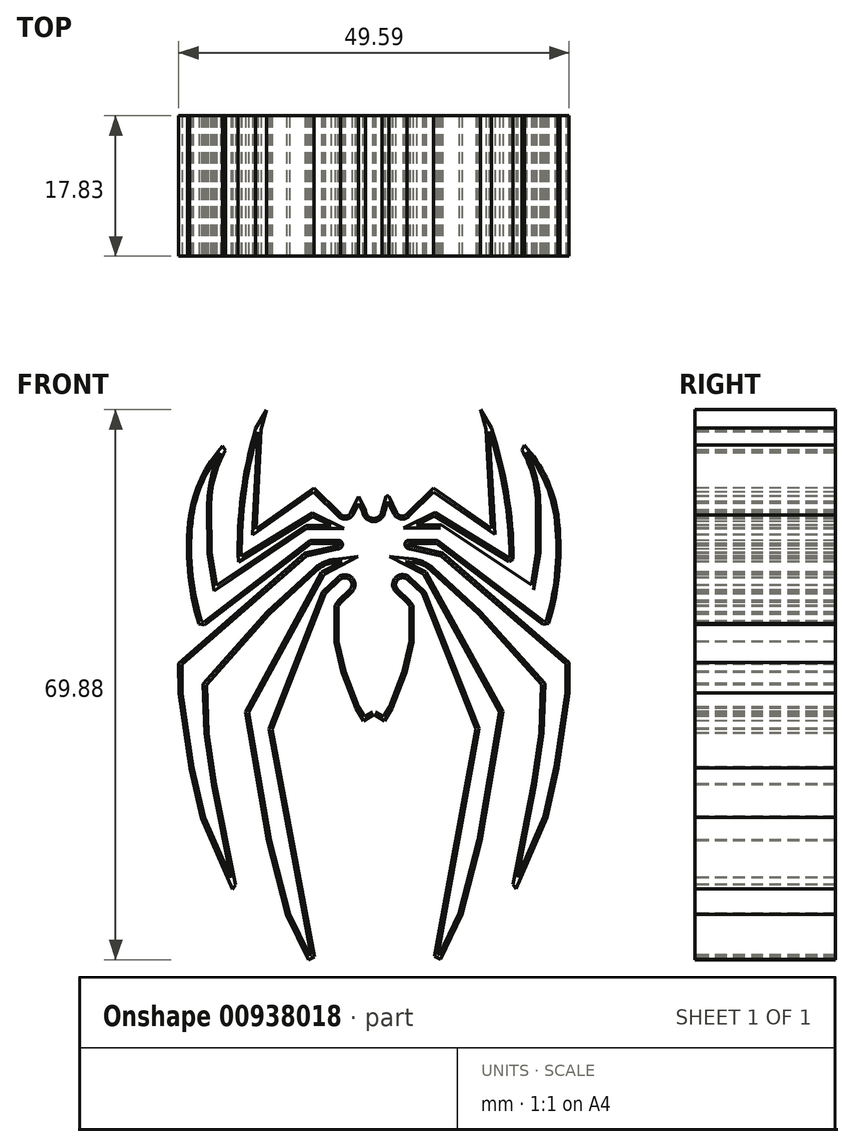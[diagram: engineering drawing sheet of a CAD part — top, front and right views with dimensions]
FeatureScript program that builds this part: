
annotation { "Feature Type Name" : "Feature", "Feature Type Description" : "" }
export const myFeature = defineFeature(function(context is Context, id is Id, definition is map)
    precondition{}
    {
        {
            var Q0;
            Q0=qCreatedBy(makeId("Front.planeOp"),FACE);
            var sketch = newSketch(context, id + "F0", { "sketchPlane" : qUnion([Q0])});
            skArc(sketch, "E0", {"start": v(10.3, 43.39) * mm, "mid": v(11.32, 42.32) * mm, "end": v(12.36, 43.36) * mm});
            skLineSegment(sketch, "E1", {"start": v(12.36, 43.36) * mm, "end": v(12.91, 45.08) * mm});
            skLineSegment(sketch, "E2", {"start": v(10.3, 43.39) * mm, "end": v(9.41, 45.08) * mm});
            skArc(sketch, "E3", {"start": v(13.25, 45.08) * mm, "mid": v(13.08, 45.2) * mm, "end": v(12.91, 45.08) * mm});
            skLineSegment(sketch, "E4", {"start": v(13.25, 45.08) * mm, "end": v(14.26, 43.06) * mm});
            skArc(sketch, "E5", {"start": v(14.26, 43.06) * mm, "mid": v(14.86, 42.62) * mm, "end": v(15.56, 42.87) * mm});
            skLineSegment(sketch, "E6", {"start": v(15.56, 42.87) * mm, "end": v(18.91, 46.2) * mm});
            skLineSegment(sketch, "E7", {"start": v(18.91, 46.2) * mm, "end": v(26.28, 41.06) * mm});
            skLineSegment(sketch, "E8", {"start": v(26.28, 41.06) * mm, "end": v(25.6, 53.69) * mm});
            skLineSegment(sketch, "E9", {"start": v(25.6, 53.69) * mm, "end": v(24.88, 56.14) * mm});
            skLineSegment(sketch, "E10", {"start": v(24.88, 56.14) * mm, "end": v(26.28, 53.79) * mm});
            skArc(sketch, "E11", {"start": v(29.06, 37.18) * mm, "mid": v(28.32, 45.6) * mm, "end": v(26.28, 53.79) * mm});
            skLineSegment(sketch, "E12", {"start": v(29.06, 37.18) * mm, "end": v(28.54, 36.84) * mm});
            skLineSegment(sketch, "E13", {"start": v(28.54, 36.84) * mm, "end": v(19.08, 42.61) * mm});
            skLineSegment(sketch, "E14", {"start": v(19.08, 42.61) * mm, "end": v(16.77, 41.46) * mm});
            skLineSegment(sketch, "E15", {"start": v(16.77, 41.46) * mm, "end": v(19.96, 41.46) * mm});
            skLineSegment(sketch, "E16", {"start": v(19.96, 41.46) * mm, "end": v(31.36, 33.86) * mm});
            skLineSegment(sketch, "E17", {"start": v(31.36, 33.86) * mm, "end": v(32.04, 38) * mm});
            skLineSegment(sketch, "E18", {"start": v(32.04, 38) * mm, "end": v(32.04, 43.9) * mm});
            skArc(sketch, "E19", {"start": v(32.04, 43.9) * mm, "mid": v(31.55, 47.6) * mm, "end": v(30.14, 51.03) * mm});
            skLineSegment(sketch, "E20", {"start": v(30.14, 51.03) * mm, "end": v(30.48, 51.61) * mm});
            skArc(sketch, "E21", {"start": v(34.72, 42.74) * mm, "mid": v(33.26, 47.5) * mm, "end": v(30.48, 51.61) * mm});
            skArc(sketch, "E22", {"start": v(33.56, 29) * mm, "mid": v(34.89, 35.8) * mm, "end": v(34.72, 42.74) * mm});
            skLineSegment(sketch, "E23", {"start": v(33.56, 29) * mm, "end": v(32.85, 28.84) * mm});
            skLineSegment(sketch, "E24", {"start": v(32.85, 28.84) * mm, "end": v(19.33, 39.16) * mm});
            skLineSegment(sketch, "E25", {"start": v(19.33, 39.16) * mm, "end": v(15.77, 39.16) * mm});
            skArc(sketch, "E26", {"start": v(15.77, 39.16) * mm, "mid": v(15.73, 38.94) * mm, "end": v(15.94, 38.86) * mm});
            skLineSegment(sketch, "E27", {"start": v(15.94, 38.86) * mm, "end": v(20.06, 37.93) * mm});
            skLineSegment(sketch, "E28", {"start": v(20.06, 37.93) * mm, "end": v(36.16, 24.01) * mm});
            skLineSegment(sketch, "E29", {"start": v(36.16, 24.01) * mm, "end": v(36.16, 20.15) * mm});
            skLineSegment(sketch, "E30", {"start": v(36.16, 20.15) * mm, "end": v(34.77, 10.65) * mm});
            skLineSegment(sketch, "E31", {"start": v(34.77, 10.65) * mm, "end": v(33.34, 4.32) * mm});
            skLineSegment(sketch, "E32", {"start": v(33.34, 4.32) * mm, "end": v(29.4, -4.75) * mm});
            skLineSegment(sketch, "E33", {"start": v(29.4, -4.75) * mm, "end": v(29.05, -4.2) * mm});
            skLineSegment(sketch, "E34", {"start": v(29.05, -4.2) * mm, "end": v(31.52, 8.6) * mm});
            skLineSegment(sketch, "E35", {"start": v(31.52, 8.6) * mm, "end": v(32.48, 15.1) * mm});
            skLineSegment(sketch, "E36", {"start": v(32.48, 15.1) * mm, "end": v(32.67, 21.21) * mm});
            skLineSegment(sketch, "E37", {"start": v(32.67, 21.21) * mm, "end": v(24.64, 30.19) * mm});
            skLineSegment(sketch, "E38", {"start": v(24.64, 30.19) * mm, "end": v(18.7, 35.66) * mm});
            skArc(sketch, "E39", {"start": v(18.7, 35.66) * mm, "mid": v(17.59, 36.4) * mm, "end": v(16.31, 36.75) * mm});
            skLineSegment(sketch, "E40", {"start": v(16.31, 36.75) * mm, "end": v(15.4, 36.86) * mm});
            skLineSegment(sketch, "E41", {"start": v(15.4, 36.86) * mm, "end": v(17.97, 35.54) * mm});
            skLineSegment(sketch, "E42", {"start": v(17.97, 35.54) * mm, "end": v(27.73, 17.79) * mm});
            skLineSegment(sketch, "E43", {"start": v(27.73, 17.79) * mm, "end": v(24.98, 1.38) * mm});
            skLineSegment(sketch, "E44", {"start": v(24.98, 1.38) * mm, "end": v(22.56, -7.98) * mm});
            skLineSegment(sketch, "E45", {"start": v(22.56, -7.98) * mm, "end": v(19.82, -13.7) * mm});
            skLineSegment(sketch, "E46", {"start": v(19.82, -13.7) * mm, "end": v(19.04, -13.34) * mm});
            skLineSegment(sketch, "E47", {"start": v(19.04, -13.34) * mm, "end": v(24.33, 15.59) * mm});
            skLineSegment(sketch, "E48", {"start": v(24.33, 15.59) * mm, "end": v(17.56, 32.78) * mm});
            skLineSegment(sketch, "E49", {"start": v(17.56, 32.78) * mm, "end": v(15.62, 34.56) * mm});
            skArc(sketch, "E50", {"start": v(15.62, 34.56) * mm, "mid": v(14.37, 34.51) * mm, "end": v(14.4, 33.26) * mm});
            skLineSegment(sketch, "E51", {"start": v(14.4, 33.26) * mm, "end": v(15.83, 31.92) * mm});
            skLineSegment(sketch, "E52", {"start": v(15.83, 31.92) * mm, "end": v(16.3, 31.27) * mm});
            skLineSegment(sketch, "E53", {"start": v(16.3, 31.27) * mm, "end": v(16.3, 26.63) * mm});
            skLineSegment(sketch, "E54", {"start": v(16.3, 26.63) * mm, "end": v(15.44, 22.78) * mm});
            skLineSegment(sketch, "E55", {"start": v(15.44, 22.78) * mm, "end": v(13.67, 18.2) * mm});
            skLineSegment(sketch, "E56", {"start": v(13.67, 18.2) * mm, "end": v(12.73, 16.61) * mm});
            skLineSegment(sketch, "E57", {"start": v(12.73, 16.61) * mm, "end": v(11.38, 17.4) * mm});
            skLineSegment(sketch, "E58.MirrorCS", {"start": v(9.41, 45.08) * mm, "end": v(8.4, 43.05) * mm});
            skArc(sketch, "E59.MirrorCS", {"start": v(8.4, 43.05) * mm, "mid": v(7.8, 42.61) * mm, "end": v(7.11, 42.86) * mm});
            skLineSegment(sketch, "E60.MirrorCS", {"start": v(7.11, 42.86) * mm, "end": v(3.74, 46.16) * mm});
            skLineSegment(sketch, "E61.MirrorCS", {"start": v(3.74, 46.16) * mm, "end": v(-3.6, 41) * mm});
            skLineSegment(sketch, "E62.MirrorCS", {"start": v(-3.6, 41) * mm, "end": v(-2.97, 53.64) * mm});
            skLineSegment(sketch, "E63.MirrorCS", {"start": v(-2.97, 53.64) * mm, "end": v(-2.26, 56.09) * mm});
            skLineSegment(sketch, "E64.MirrorCS", {"start": v(-2.26, 56.09) * mm, "end": v(-3.65, 53.73) * mm});
            skArc(sketch, "E65.MirrorCS", {"start": v(-5.85, 36.78) * mm, "mid": v(-5.43, 45.34) * mm, "end": v(-3.65, 53.73) * mm});
            skLineSegment(sketch, "E66.MirrorCS", {"start": v(-5.85, 36.78) * mm, "end": v(3.6, 42.59) * mm});
            skLineSegment(sketch, "E67.MirrorCS", {"start": v(3.6, 42.59) * mm, "end": v(5.9, 41.44) * mm});
            skLineSegment(sketch, "E68.MirrorCS", {"start": v(5.9, 41.44) * mm, "end": v(2.71, 41.43) * mm});
            skLineSegment(sketch, "E69.MirrorCS", {"start": v(2.71, 41.43) * mm, "end": v(-8.66, 33.79) * mm});
            skLineSegment(sketch, "E70.MirrorCS", {"start": v(-8.66, 33.79) * mm, "end": v(-9.35, 37.93) * mm});
            skLineSegment(sketch, "E71.MirrorCS", {"start": v(-9.35, 37.93) * mm, "end": v(-9.38, 43.83) * mm});
            skArc(sketch, "E72.MirrorCS", {"start": v(-9.38, 43.83) * mm, "mid": v(-8.9, 47.52) * mm, "end": v(-7.5, 50.96) * mm});
            skLineSegment(sketch, "E73.MirrorCS", {"start": v(-7.5, 50.96) * mm, "end": v(-7.85, 51.55) * mm});
            skArc(sketch, "E74.MirrorCS", {"start": v(-12.05, 42.65) * mm, "mid": v(-10.61, 47.41) * mm, "end": v(-7.85, 51.55) * mm});
            skArc(sketch, "E75.MirrorCS", {"start": v(-10.85, 28.92) * mm, "mid": v(-12.2, 35.72) * mm, "end": v(-12.05, 42.65) * mm});
            skLineSegment(sketch, "E76.MirrorCS", {"start": v(-10.85, 28.92) * mm, "end": v(-10.13, 28.77) * mm});
            skLineSegment(sketch, "E77.MirrorCS", {"start": v(-10.13, 28.77) * mm, "end": v(3.35, 39.13) * mm});
            skLineSegment(sketch, "E78.MirrorCS", {"start": v(3.35, 39.13) * mm, "end": v(6.91, 39.14) * mm});
            skArc(sketch, "E79.MirrorCS", {"start": v(6.91, 39.14) * mm, "mid": v(6.95, 38.92) * mm, "end": v(6.74, 38.85) * mm});
            skLineSegment(sketch, "E80.MirrorCS", {"start": v(6.74, 38.85) * mm, "end": v(2.62, 37.9) * mm});
            skLineSegment(sketch, "E81.MirrorCS", {"start": v(2.62, 37.9) * mm, "end": v(-13.43, 23.92) * mm});
            skLineSegment(sketch, "E82.MirrorCS", {"start": v(-13.43, 23.92) * mm, "end": v(-13.41, 20.06) * mm});
            skLineSegment(sketch, "E83.MirrorCS", {"start": v(-13.41, 20.06) * mm, "end": v(-11.99, 10.57) * mm});
            skLineSegment(sketch, "E84.MirrorCS", {"start": v(-11.99, 10.57) * mm, "end": v(-10.54, 4.24) * mm});
            skLineSegment(sketch, "E85.MirrorCS", {"start": v(-10.54, 4.24) * mm, "end": v(-6.57, -4.82) * mm});
            skLineSegment(sketch, "E86.MirrorCS", {"start": v(-6.57, -4.82) * mm, "end": v(-6.22, -4.26) * mm});
            skLineSegment(sketch, "E87.MirrorCS", {"start": v(-6.22, -4.26) * mm, "end": v(-8.73, 8.52) * mm});
            skLineSegment(sketch, "E88.MirrorCS", {"start": v(-8.73, 8.52) * mm, "end": v(-9.72, 15.02) * mm});
            skLineSegment(sketch, "E89.MirrorCS", {"start": v(-9.72, 15.02) * mm, "end": v(-9.93, 21.14) * mm});
            skLineSegment(sketch, "E90.MirrorCS", {"start": v(-9.93, 21.14) * mm, "end": v(-1.93, 30.14) * mm});
            skLineSegment(sketch, "E91.MirrorCS", {"start": v(-1.93, 30.14) * mm, "end": v(4, 35.64) * mm});
            skArc(sketch, "E92.MirrorCS", {"start": v(4, 35.64) * mm, "mid": v(5.1, 36.38) * mm, "end": v(6.37, 36.74) * mm});
            skLineSegment(sketch, "E93.MirrorCS", {"start": v(6.37, 36.74) * mm, "end": v(7.3, 36.84) * mm});
            skLineSegment(sketch, "E94.MirrorCS", {"start": v(7.3, 36.84) * mm, "end": v(4.72, 35.52) * mm});
            skLineSegment(sketch, "E95.MirrorCS", {"start": v(4.72, 35.52) * mm, "end": v(-4.98, 17.73) * mm});
            skLineSegment(sketch, "E96.MirrorCS", {"start": v(-4.98, 17.73) * mm, "end": v(-2.17, 1.33) * mm});
            skLineSegment(sketch, "E97.MirrorCS", {"start": v(-2.17, 1.33) * mm, "end": v(0.29, -8.02) * mm});
            skLineSegment(sketch, "E98.MirrorCS", {"start": v(0.29, -8.02) * mm, "end": v(3.05, -13.74) * mm});
            skLineSegment(sketch, "E99.MirrorCS", {"start": v(3.05, -13.74) * mm, "end": v(3.83, -13.37) * mm});
            skLineSegment(sketch, "E100.MirrorCS", {"start": v(3.83, -13.37) * mm, "end": v(-1.57, 15.54) * mm});
            skLineSegment(sketch, "E101.MirrorCS", {"start": v(-1.57, 15.54) * mm, "end": v(5.15, 32.75) * mm});
            skLineSegment(sketch, "E102.MirrorCS", {"start": v(5.15, 32.75) * mm, "end": v(7.08, 34.54) * mm});
            skArc(sketch, "E103.MirrorCS", {"start": v(7.08, 34.54) * mm, "mid": v(8.33, 34.5) * mm, "end": v(8.3, 33.25) * mm});
            skLineSegment(sketch, "E104.MirrorCS", {"start": v(8.3, 33.25) * mm, "end": v(6.87, 31.9) * mm});
            skLineSegment(sketch, "E105.MirrorCS", {"start": v(6.87, 31.9) * mm, "end": v(6.4, 31.25) * mm});
            skLineSegment(sketch, "E106.MirrorCS", {"start": v(6.4, 31.25) * mm, "end": v(6.42, 26.6) * mm});
            skLineSegment(sketch, "E107.MirrorCS", {"start": v(6.42, 26.6) * mm, "end": v(7.3, 22.76) * mm});
            skLineSegment(sketch, "E108.MirrorCS", {"start": v(7.3, 22.76) * mm, "end": v(9.08, 18.2) * mm});
            skLineSegment(sketch, "E109.MirrorCS", {"start": v(9.08, 18.2) * mm, "end": v(10.03, 16.6) * mm});
            skLineSegment(sketch, "E110.MirrorCS", {"start": v(10.03, 16.6) * mm, "end": v(11.37, 17.4) * mm});
            skLineSegment(sketch, "E111.0", {"start": v(12.6, 17.14) * mm, "end": v(11.58, 17.74) * mm});
            skLineSegment(sketch, "E111.1", {"start": v(13.32, 18.38) * mm, "end": v(12.6, 17.14) * mm});
            skLineSegment(sketch, "E111.2", {"start": v(15.07, 22.89) * mm, "end": v(13.32, 18.38) * mm});
            skLineSegment(sketch, "E111.3", {"start": v(15.92, 26.67) * mm, "end": v(15.07, 22.89) * mm});
            skLineSegment(sketch, "E111.4", {"start": v(15.92, 31.14) * mm, "end": v(15.92, 26.67) * mm});
            skLineSegment(sketch, "E111.5", {"start": v(15.54, 31.66) * mm, "end": v(15.92, 31.14) * mm});
            skLineSegment(sketch, "E111.6", {"start": v(3.7, 45.66) * mm, "end": v(-4.03, 40.23) * mm});
            skLineSegment(sketch, "E111.7", {"start": v(-4.03, 40.23) * mm, "end": v(-3.38, 53.3) * mm});
            skArc(sketch, "E111.8", {"start": v(-5.48, 37.46) * mm, "mid": v(-5.02, 45.46) * mm, "end": v(-3.38, 53.3) * mm});
            skLineSegment(sketch, "E111.9", {"start": v(-5.48, 37.46) * mm, "end": v(3.57, 43.03) * mm});
            skLineSegment(sketch, "E111.10", {"start": v(3.57, 43.03) * mm, "end": v(7.54, 41.06) * mm});
            skLineSegment(sketch, "E111.11", {"start": v(7.54, 41.06) * mm, "end": v(2.83, 41.04) * mm});
            skLineSegment(sketch, "E111.12", {"start": v(2.83, 41.04) * mm, "end": v(-8.94, 33.13) * mm});
            skLineSegment(sketch, "E111.13", {"start": v(-8.94, 33.13) * mm, "end": v(-9.74, 37.9) * mm});
            skLineSegment(sketch, "E111.14", {"start": v(-9.74, 37.9) * mm, "end": v(-9.76, 43.83) * mm});
            skArc(sketch, "E111.15", {"start": v(-9.76, 43.83) * mm, "mid": v(-9.35, 47.34) * mm, "end": v(-8.1, 50.66) * mm});
            skArc(sketch, "E111.16", {"start": v(-11.67, 42.6) * mm, "mid": v(-10.43, 46.87) * mm, "end": v(-8.1, 50.66) * mm});
            skArc(sketch, "E111.17", {"start": v(-10.55, 29.25) * mm, "mid": v(-11.82, 35.86) * mm, "end": v(-11.67, 42.6) * mm});
            skLineSegment(sketch, "E111.18", {"start": v(-10.55, 29.25) * mm, "end": v(-10.23, 29.18) * mm});
            skLineSegment(sketch, "E111.19", {"start": v(-10.23, 29.18) * mm, "end": v(3.22, 39.52) * mm});
            skLineSegment(sketch, "E111.20", {"start": v(3.22, 39.52) * mm, "end": v(7, 39.53) * mm});
            skArc(sketch, "E111.21", {"start": v(7, 39.53) * mm, "mid": v(7.35, 38.88) * mm, "end": v(6.75, 38.45) * mm});
            skLineSegment(sketch, "E111.22", {"start": v(6.75, 38.45) * mm, "end": v(2.8, 37.55) * mm});
            skLineSegment(sketch, "E111.23", {"start": v(2.8, 37.55) * mm, "end": v(-13.04, 23.75) * mm});
            skLineSegment(sketch, "E111.24", {"start": v(-13.04, 23.75) * mm, "end": v(-13.03, 20.1) * mm});
            skLineSegment(sketch, "E111.25", {"start": v(-13.03, 20.1) * mm, "end": v(-11.6, 10.64) * mm});
            skLineSegment(sketch, "E111.26", {"start": v(-11.6, 10.64) * mm, "end": v(-10.17, 4.36) * mm});
            skLineSegment(sketch, "E111.27", {"start": v(-10.17, 4.36) * mm, "end": v(-6.79, -3.36) * mm});
            skLineSegment(sketch, "E111.28", {"start": v(-6.79, -3.36) * mm, "end": v(-9.11, 8.45) * mm});
            skLineSegment(sketch, "E111.29", {"start": v(-9.11, 8.45) * mm, "end": v(-10.1, 14.98) * mm});
            skLineSegment(sketch, "E111.30", {"start": v(-1.97, 15.58) * mm, "end": v(4.82, 32.98) * mm});
            skLineSegment(sketch, "E111.31", {"start": v(4.82, 32.98) * mm, "end": v(6.81, 34.83) * mm});
            skArc(sketch, "E111.32", {"start": v(6.81, 34.83) * mm, "mid": v(8.6, 34.76) * mm, "end": v(8.56, 32.97) * mm});
            skLineSegment(sketch, "E111.33", {"start": v(8.56, 32.97) * mm, "end": v(7.17, 31.64) * mm});
            skLineSegment(sketch, "E111.34", {"start": v(7.17, 31.64) * mm, "end": v(6.8, 31.13) * mm});
            skLineSegment(sketch, "E111.35", {"start": v(6.8, 31.13) * mm, "end": v(6.8, 26.65) * mm});
            skLineSegment(sketch, "E111.36", {"start": v(10.16, 17.14) * mm, "end": v(11.17, 17.74) * mm});
            skLineSegment(sketch, "E111.37", {"start": v(9.43, 18.37) * mm, "end": v(10.16, 17.14) * mm});
            skLineSegment(sketch, "E111.38", {"start": v(7.67, 22.87) * mm, "end": v(9.43, 18.37) * mm});
            skLineSegment(sketch, "E111.39", {"start": v(6.8, 26.65) * mm, "end": v(7.67, 22.87) * mm});
            skLineSegment(sketch, "E111.40", {"start": v(3.4, -13.15) * mm, "end": v(-1.97, 15.58) * mm});
            skLineSegment(sketch, "E111.41", {"start": v(3.23, -13.22) * mm, "end": v(3.4, -13.15) * mm});
            skLineSegment(sketch, "E111.42", {"start": v(0.65, -7.88) * mm, "end": v(3.23, -13.22) * mm});
            skLineSegment(sketch, "E111.43", {"start": v(-1.79, 1.42) * mm, "end": v(0.65, -7.88) * mm});
            skLineSegment(sketch, "E111.44", {"start": v(-4.57, 17.66) * mm, "end": v(-1.79, 1.42) * mm});
            skLineSegment(sketch, "E111.45", {"start": v(5, 35.23) * mm, "end": v(-4.57, 17.66) * mm});
            skLineSegment(sketch, "E111.46", {"start": v(9.36, 37.48) * mm, "end": v(5, 35.23) * mm});
            skLineSegment(sketch, "E111.47", {"start": v(6.33, 37.12) * mm, "end": v(9.36, 37.48) * mm});
            skArc(sketch, "E111.48", {"start": v(3.74, 35.92) * mm, "mid": v(4.94, 36.73) * mm, "end": v(6.33, 37.12) * mm});
            skLineSegment(sketch, "E111.49", {"start": v(-2.2, 30.41) * mm, "end": v(3.74, 35.92) * mm});
            skLineSegment(sketch, "E111.50", {"start": v(-10.32, 21.28) * mm, "end": v(-2.2, 30.41) * mm});
            skLineSegment(sketch, "E111.51", {"start": v(-10.1, 14.98) * mm, "end": v(-10.32, 21.28) * mm});
            skLineSegment(sketch, "E111.52", {"start": v(6.83, 42.59) * mm, "end": v(3.7, 45.66) * mm});
            skArc(sketch, "E111.53", {"start": v(8.75, 42.88) * mm, "mid": v(7.87, 42.23) * mm, "end": v(6.83, 42.59) * mm});
            skLineSegment(sketch, "E111.54", {"start": v(9.42, 44.23) * mm, "end": v(8.75, 42.88) * mm});
            skLineSegment(sketch, "E111.55", {"start": v(9.92, 43.29) * mm, "end": v(9.42, 44.23) * mm});
            skArc(sketch, "E111.56", {"start": v(9.92, 43.29) * mm, "mid": v(11.33, 41.93) * mm, "end": v(12.75, 43.3) * mm});
            skLineSegment(sketch, "E111.57", {"start": v(12.75, 43.3) * mm, "end": v(13.12, 44.46) * mm});
            skLineSegment(sketch, "E111.58", {"start": v(13.12, 44.46) * mm, "end": v(13.91, 42.88) * mm});
            skArc(sketch, "E111.59", {"start": v(13.91, 42.88) * mm, "mid": v(14.8, 42.24) * mm, "end": v(15.83, 42.6) * mm});
            skLineSegment(sketch, "E111.60", {"start": v(15.83, 42.6) * mm, "end": v(18.96, 45.69) * mm});
            skLineSegment(sketch, "E111.61", {"start": v(18.96, 45.69) * mm, "end": v(26.7, 40.29) * mm});
            skLineSegment(sketch, "E111.62", {"start": v(26.7, 40.29) * mm, "end": v(26, 53.39) * mm});
            skArc(sketch, "E111.63", {"start": v(28.67, 37.39) * mm, "mid": v(27.94, 45.49) * mm, "end": v(26, 53.39) * mm});
            skLineSegment(sketch, "E111.64", {"start": v(28.67, 37.39) * mm, "end": v(28.53, 37.3) * mm});
            skLineSegment(sketch, "E111.65", {"start": v(28.53, 37.3) * mm, "end": v(19.1, 43.06) * mm});
            skLineSegment(sketch, "E111.66", {"start": v(19.1, 43.06) * mm, "end": v(15.13, 41.07) * mm});
            skLineSegment(sketch, "E111.67", {"start": v(15.13, 41.07) * mm, "end": v(19.84, 41.07) * mm});
            skLineSegment(sketch, "E111.68", {"start": v(19.84, 41.07) * mm, "end": v(31.64, 33.2) * mm});
            skLineSegment(sketch, "E111.69", {"start": v(31.64, 33.2) * mm, "end": v(32.42, 37.97) * mm});
            skLineSegment(sketch, "E111.70", {"start": v(32.42, 37.97) * mm, "end": v(32.42, 43.9) * mm});
            skArc(sketch, "E111.71", {"start": v(32.42, 43.9) * mm, "mid": v(32, 47.42) * mm, "end": v(30.74, 50.73) * mm});
            skArc(sketch, "E111.72", {"start": v(34.34, 42.68) * mm, "mid": v(33.09, 46.95) * mm, "end": v(30.74, 50.73) * mm});
            skArc(sketch, "E111.73", {"start": v(33.26, 29.33) * mm, "mid": v(34.51, 35.95) * mm, "end": v(34.34, 42.68) * mm});
            skLineSegment(sketch, "E111.74", {"start": v(33.26, 29.33) * mm, "end": v(32.94, 29.26) * mm});
            skLineSegment(sketch, "E111.75", {"start": v(32.94, 29.26) * mm, "end": v(19.46, 39.54) * mm});
            skLineSegment(sketch, "E111.76", {"start": v(19.46, 39.54) * mm, "end": v(15.67, 39.54) * mm});
            skArc(sketch, "E111.77", {"start": v(15.67, 39.54) * mm, "mid": v(15.33, 38.89) * mm, "end": v(15.94, 38.47) * mm});
            skLineSegment(sketch, "E111.78", {"start": v(15.94, 38.47) * mm, "end": v(19.88, 37.58) * mm});
            skLineSegment(sketch, "E111.79", {"start": v(19.88, 37.58) * mm, "end": v(35.77, 23.83) * mm});
            skLineSegment(sketch, "E111.80", {"start": v(35.77, 23.83) * mm, "end": v(35.77, 20.18) * mm});
            skLineSegment(sketch, "E111.81", {"start": v(35.77, 20.18) * mm, "end": v(34.39, 10.72) * mm});
            skLineSegment(sketch, "E111.82", {"start": v(34.39, 10.72) * mm, "end": v(32.97, 4.44) * mm});
            skLineSegment(sketch, "E111.83", {"start": v(32.97, 4.44) * mm, "end": v(29.62, -3.3) * mm});
            skLineSegment(sketch, "E111.84", {"start": v(29.62, -3.3) * mm, "end": v(31.9, 8.53) * mm});
            skLineSegment(sketch, "E111.85", {"start": v(31.9, 8.53) * mm, "end": v(32.87, 15.06) * mm});
            skLineSegment(sketch, "E111.86", {"start": v(32.87, 15.06) * mm, "end": v(33.07, 21.36) * mm});
            skLineSegment(sketch, "E111.87", {"start": v(33.07, 21.36) * mm, "end": v(24.92, 30.46) * mm});
            skLineSegment(sketch, "E111.88", {"start": v(24.92, 30.46) * mm, "end": v(18.96, 35.95) * mm});
            skArc(sketch, "E111.89", {"start": v(18.96, 35.95) * mm, "mid": v(17.75, 36.75) * mm, "end": v(16.36, 37.14) * mm});
            skLineSegment(sketch, "E111.90", {"start": v(16.36, 37.14) * mm, "end": v(13.32, 37.49) * mm});
            skLineSegment(sketch, "E111.91", {"start": v(13.32, 37.49) * mm, "end": v(17.69, 35.25) * mm});
            skLineSegment(sketch, "E111.92", {"start": v(17.69, 35.25) * mm, "end": v(27.33, 17.72) * mm});
            skLineSegment(sketch, "E111.93", {"start": v(27.33, 17.72) * mm, "end": v(24.6, 1.46) * mm});
            skLineSegment(sketch, "E111.94", {"start": v(24.6, 1.46) * mm, "end": v(22.2, -7.85) * mm});
            skLineSegment(sketch, "E111.95", {"start": v(22.2, -7.85) * mm, "end": v(19.63, -13.2) * mm});
            skLineSegment(sketch, "E111.96", {"start": v(19.63, -13.2) * mm, "end": v(19.47, -13.12) * mm});
            skLineSegment(sketch, "E111.97", {"start": v(19.47, -13.12) * mm, "end": v(24.73, 15.62) * mm});
            skLineSegment(sketch, "E111.98", {"start": v(24.73, 15.62) * mm, "end": v(17.88, 33) * mm});
            skLineSegment(sketch, "E111.99", {"start": v(17.88, 33) * mm, "end": v(15.88, 34.84) * mm});
            skArc(sketch, "E111.100", {"start": v(15.88, 34.84) * mm, "mid": v(14.09, 34.77) * mm, "end": v(14.14, 32.98) * mm});
            skLineSegment(sketch, "E111.101", {"start": v(14.14, 32.98) * mm, "end": v(15.54, 31.66) * mm});
            skSolve(sketch);
        }
        {
            var Q0;
            Q0 = qSketchRegion(id + "F0", true);
            var Q1;
            Q1=sQuery(id+"F0.wireOp",EDGE,"E111.72");
            var Q2;
            Q2=sQuery(id+"F0.wireOp",EDGE,"E21");
            var Q3;
            Q3=sQuery(id+"F0.wireOp",EDGE,"E111.73");
            var Q4;
            Q4=sQuery(id+"F0.wireOp",EDGE,"E22");
            var Q5;
            Q5=sQuery(id+"F0.wireOp",EDGE,"E111.71");
            var Q6;
            Q6=sQuery(id+"F0.wireOp",EDGE,"E20");
            var Q7;
            Q7=sQuery(id+"F0.wireOp",EDGE,"E111.45");
            var Q8;
            Q8=sQuery(id+"F0.wireOp",EDGE,"E111.93");
            var Q9;
            Q9=sQuery(id+"F0.wireOp",EDGE,"E53");
            var Q10;
            Q10=sQuery(id+"F0.wireOp",EDGE,"E111.6");
            var Q11;
            Q11=sQuery(id+"F0.wireOp",EDGE,"E81.MirrorCS");
            var Q12;
            Q12=sQuery(id+"F0.wireOp",EDGE,"E111.2");
            var Q13;
            Q13=sQuery(id+"F0.wireOp",EDGE,"E17");
            var Q14;
            Q14=sQuery(id+"F0.wireOp",EDGE,"E111.30");
            var Q15;
            Q15=sQuery(id+"F0.wireOp",EDGE,"E111.69");
            var Q16;
            Q16=sQuery(id+"F0.wireOp",EDGE,"E29");
            var Q17;
            Q17=sQuery(id+"F0.wireOp",EDGE,"E111.13");
            var Q18;
            Q18=sQuery(id+"F0.wireOp",EDGE,"E111.98");
            var Q19;
            Q19=sQuery(id+"F0.wireOp",EDGE,"E111.94");
            var Q20;
            Q20=sQuery(id+"F0.wireOp",EDGE,"E37");
            var Q21;
            Q21=sQuery(id+"F0.wireOp",EDGE,"E111.25");
            var Q22;
            Q22=sQuery(id+"F0.wireOp",EDGE,"E24");
            var Q23;
            Q23=sQuery(id+"F0.wireOp",EDGE,"E111.50");
            var Q24;
            Q24=sQuery(id+"F0.wireOp",EDGE,"E111.38");
            var Q25;
            Q25=sQuery(id+"F0.wireOp",EDGE,"E97.MirrorCS");
            var Q26;
            Q26=sQuery(id+"F0.wireOp",EDGE,"E16");
            var Q27;
            Q27=sQuery(id+"F0.wireOp",EDGE,"E48");
            var Q28;
            Q28=sQuery(id+"F0.wireOp",EDGE,"E85.MirrorCS");
            var Q29;
            Q29=sQuery(id+"F0.wireOp",EDGE,"E32");
            var Q30;
            Q30=sQuery(id+"F0.wireOp",EDGE,"E108.MirrorCS");
            var Q31;
            Q31=sQuery(id+"F0.wireOp",EDGE,"E111.14");
            var Q32;
            Q32=sQuery(id+"F0.wireOp",EDGE,"E111.29");
            var Q33;
            Q33=sQuery(id+"F0.wireOp",EDGE,"E111.62");
            var Q34;
            Q34=sQuery(id+"F0.wireOp",EDGE,"E65.MirrorCS");
            var Q35;
            Q35=sQuery(id+"F0.wireOp",EDGE,"E44");
            var Q36;
            Q36=sQuery(id+"F0.wireOp",EDGE,"E96.MirrorCS");
            var Q37;
            Q37=sQuery(id+"F0.wireOp",EDGE,"E111.15");
            var Q38;
            Q38=sQuery(id+"F0.wireOp",EDGE,"E55");
            var Q39;
            Q39=sQuery(id+"F0.wireOp",EDGE,"E88.MirrorCS");
            var Q40;
            Q40=sQuery(id+"F0.wireOp",EDGE,"E72.MirrorCS");
            var Q41;
            Q41=sQuery(id+"F0.wireOp",EDGE,"E111.85");
            var Q42;
            Q42=sQuery(id+"F0.wireOp",EDGE,"E61.MirrorCS");
            var Q43;
            Q43=sQuery(id+"F0.wireOp",EDGE,"E77.MirrorCS");
            var Q44;
            Q44=sQuery(id+"F0.wireOp",EDGE,"E111.8");
            var Q45;
            Q45=sQuery(id+"F0.wireOp",EDGE,"E101.MirrorCS");
            var Q46;
            Q46=sQuery(id+"F0.wireOp",EDGE,"E111.24");
            var Q47;
            Q47=sQuery(id+"F0.wireOp",EDGE,"E111.95");
            var Q48;
            Q48=sQuery(id+"F0.wireOp",EDGE,"E111.82");
            var Q49;
            Q49=sQuery(id+"F0.wireOp",EDGE,"E62.MirrorCS");
            var Q50;
            Q50=sQuery(id+"F0.wireOp",EDGE,"E69.MirrorCS");
            var Q51;
            Q51=sQuery(id+"F0.wireOp",EDGE,"E84.MirrorCS");
            var Q52;
            Q52=sQuery(id+"F0.wireOp",EDGE,"E45");
            var Q53;
            Q53=sQuery(id+"F0.wireOp",EDGE,"E111.88");
            var Q54;
            Q54=sQuery(id+"F0.wireOp",EDGE,"E36");
            var Q55;
            Q55=sQuery(id+"F0.wireOp",EDGE,"E100.MirrorCS");
            var Q56;
            Q56=sQuery(id+"F0.wireOp",EDGE,"E111.79");
            var Q57;
            Q57=sQuery(id+"F0.wireOp",EDGE,"E111.86");
            var Q58;
            Q58=sQuery(id+"F0.wireOp",EDGE,"E30");
            var Q59;
            Q59=sQuery(id+"F0.wireOp",EDGE,"E111.9");
            var Q60;
            Q60=sQuery(id+"F0.wireOp",EDGE,"E111.40");
            var Q61;
            Q61=sQuery(id+"F0.wireOp",EDGE,"E111.61");
            var Q62;
            Q62=sQuery(id+"F0.wireOp",EDGE,"E111.70");
            var Q63;
            Q63=sQuery(id+"F0.wireOp",EDGE,"E11");
            var Q64;
            Q64=sQuery(id+"F0.wireOp",EDGE,"E111.23");
            var Q65;
            Q65=sQuery(id+"F0.wireOp",EDGE,"E31");
            var Q66;
            Q66=sQuery(id+"F0.wireOp",EDGE,"E35");
            var Q67;
            Q67=sQuery(id+"F0.wireOp",EDGE,"E111.26");
            var Q68;
            Q68=sQuery(id+"F0.wireOp",EDGE,"E7");
            var Q69;
            Q69=sQuery(id+"F0.wireOp",EDGE,"E95.MirrorCS");
            var Q70;
            Q70=sQuery(id+"F0.wireOp",EDGE,"E43");
            var Q71;
            Q71=sQuery(id+"F0.wireOp",EDGE,"E111.12");
            var Q72;
            Q72=sQuery(id+"F0.wireOp",EDGE,"E75.MirrorCS");
            var Q73;
            Q73=sQuery(id+"F0.wireOp",EDGE,"E111.97");
            var Q74;
            Q74=sQuery(id+"F0.wireOp",EDGE,"E89.MirrorCS");
            var Q75;
            Q75=sQuery(id+"F0.wireOp",EDGE,"E91.MirrorCS");
            var Q76;
            Q76=sQuery(id+"F0.wireOp",EDGE,"E34");
            var Q77;
            Q77=sQuery(id+"F0.wireOp",EDGE,"E18");
            var Q78;
            Q78=sQuery(id+"F0.wireOp",EDGE,"E74.MirrorCS");
            var Q79;
            Q79=sQuery(id+"F0.wireOp",EDGE,"E98.MirrorCS");
            var Q80;
            Q80=sQuery(id+"F0.wireOp",EDGE,"E47");
            var Q81;
            Q81=sQuery(id+"F0.wireOp",EDGE,"E111.16");
            var Q82;
            Q82=sQuery(id+"F0.wireOp",EDGE,"E111.75");
            var Q83;
            Q83=sQuery(id+"F0.wireOp",EDGE,"E27");
            var Q84;
            Q84=sQuery(id+"F0.wireOp",EDGE,"E54");
            var Q85;
            Q85=sQuery(id+"F0.wireOp",EDGE,"E111.28");
            var Q86;
            Q86=sQuery(id+"F0.wireOp",EDGE,"E13");
            var Q87;
            Q87=sQuery(id+"F0.wireOp",EDGE,"E111.44");
            var Q88;
            Q88=sQuery(id+"F0.wireOp",EDGE,"E111.81");
            var Q89;
            Q89=sQuery(id+"F0.wireOp",EDGE,"E111.3");
            var Q90;
            Q90=sQuery(id+"F0.wireOp",EDGE,"E111.83");
            var Q91;
            Q91=sQuery(id+"F0.wireOp",EDGE,"E111.35");
            var Q92;
            Q92=sQuery(id+"F0.wireOp",EDGE,"E111.7");
            var Q93;
            Q93=sQuery(id+"F0.wireOp",EDGE,"E111.87");
            var Q94;
            Q94=sQuery(id+"F0.wireOp",EDGE,"E111.17");
            var Q95;
            Q95=sQuery(id+"F0.wireOp",EDGE,"E106.MirrorCS");
            var Q96;
            Q96=sQuery(id+"F0.wireOp",EDGE,"E19");
            var Q97;
            Q97=sQuery(id+"F0.wireOp",EDGE,"E70.MirrorCS");
            var Q98;
            Q98=sQuery(id+"F0.wireOp",EDGE,"E8");
            var Q99;
            Q99=sQuery(id+"F0.wireOp",EDGE,"E111.27");
            var Q100;
            Q100=sQuery(id+"F0.wireOp",EDGE,"E83.MirrorCS");
            var Q101;
            Q101=sQuery(id+"F0.wireOp",EDGE,"E38");
            var Q102;
            Q102=sQuery(id+"F0.wireOp",EDGE,"E111.65");
            var Q103;
            Q103=sQuery(id+"F0.wireOp",EDGE,"E111.43");
            var Q104;
            Q104=sQuery(id+"F0.wireOp",EDGE,"E111.49");
            var Q105;
            Q105=sQuery(id+"F0.wireOp",EDGE,"E111.19");
            var Q106;
            Q106=sQuery(id+"F0.wireOp",EDGE,"E111.92");
            var Q107;
            Q107=sQuery(id+"F0.wireOp",EDGE,"E90.MirrorCS");
            var Q108;
            Q108=sQuery(id+"F0.wireOp",EDGE,"E111.51");
            var Q109;
            Q109=sQuery(id+"F0.wireOp",EDGE,"E42");
            var Q110;
            Q110=sQuery(id+"F0.wireOp",EDGE,"E87.MirrorCS");
            var Q111;
            Q111=sQuery(id+"F0.wireOp",EDGE,"E107.MirrorCS");
            var Q112;
            Q112=sQuery(id+"F0.wireOp",EDGE,"E111.84");
            var Q113;
            Q113=sQuery(id+"F0.wireOp",EDGE,"E111.42");
            var Q114;
            Q114=sQuery(id+"F0.wireOp",EDGE,"E66.MirrorCS");
            var Q115;
            Q115=sQuery(id+"F0.wireOp",EDGE,"E111.39");
            var Q116;
            Q116=sQuery(id+"F0.wireOp",EDGE,"E111.80");
            var Q117;
            Q117=sQuery(id+"F0.wireOp",EDGE,"E111.4");
            var Q118;
            Q118=sQuery(id+"F0.wireOp",EDGE,"E82.MirrorCS");
            var Q119;
            Q119=sQuery(id+"F0.wireOp",EDGE,"E71.MirrorCS");
            var Q120;
            Q120=sQuery(id+"F0.wireOp",EDGE,"E49");
            var Q121;
            Q121=sQuery(id+"F0.wireOp",EDGE,"E111.66");
            var Q122;
            Q122=sQuery(id+"F0.wireOp",EDGE,"E111.22");
            var Q123;
            Q123=sQuery(id+"F0.wireOp",EDGE,"E103.MirrorCS");
            var Q124;
            Q124=sQuery(id+"F0.wireOp",EDGE,"E104.MirrorCS");
            var Q125;
            Q125=sQuery(id+"F0.wireOp",EDGE,"E80.MirrorCS");
            var Q126;
            Q126=sQuery(id+"F0.wireOp",EDGE,"E111.1");
            var Q127;
            Q127=sQuery(id+"F0.wireOp",EDGE,"E111.46");
            var Q128;
            Q128=sQuery(id+"F0.wireOp",EDGE,"E60.MirrorCS");
            var Q129;
            Q129=sQuery(id+"F0.wireOp",EDGE,"E33");
            var Q130;
            Q130=sQuery(id+"F0.wireOp",EDGE,"E68.MirrorCS");
            var Q131;
            Q131=sQuery(id+"F0.wireOp",EDGE,"E64.MirrorCS");
            var Q132;
            Q132=sQuery(id+"F0.wireOp",EDGE,"E111.47");
            var Q133;
            Q133=sQuery(id+"F0.wireOp",EDGE,"E78.MirrorCS");
            var Q134;
            Q134=sQuery(id+"F0.wireOp",EDGE,"E111.37");
            var Q135;
            Q135=sQuery(id+"F0.wireOp",EDGE,"E111.20");
            var Q136;
            Q136=sQuery(id+"F0.wireOp",EDGE,"E73.MirrorCS");
            var Q137;
            Q137=sQuery(id+"F0.wireOp",EDGE,"E111.60");
            var Q138;
            Q138=sQuery(id+"F0.wireOp",EDGE,"E111.91");
            var Q139;
            Q139=sQuery(id+"F0.wireOp",EDGE,"E10");
            var Q140;
            Q140=sQuery(id+"F0.wireOp",EDGE,"E111.52");
            var Q141;
            Q141=sQuery(id+"F0.wireOp",EDGE,"E111.100");
            var Q142;
            Q142=sQuery(id+"F0.wireOp",EDGE,"E111.99");
            var Q143;
            Q143=sQuery(id+"F0.wireOp",EDGE,"E2");
            var Q144;
            Q144=sQuery(id+"F0.wireOp",EDGE,"E111.11");
            var Q145;
            Q145=sQuery(id+"F0.wireOp",EDGE,"E6");
            var Q146;
            Q146=sQuery(id+"F0.wireOp",EDGE,"E86.MirrorCS");
            var Q147;
            Q147=sQuery(id+"F0.wireOp",EDGE,"E111.76");
            var Q148;
            Q148=sQuery(id+"F0.wireOp",EDGE,"E111.10");
            var Q149;
            Q149=sQuery(id+"F0.wireOp",EDGE,"E23");
            var Q150;
            Q150=sQuery(id+"F0.wireOp",EDGE,"E111.32");
            var Q151;
            Q151=sQuery(id+"F0.wireOp",EDGE,"E111.34");
            var Q152;
            Q152=sQuery(id+"F0.wireOp",EDGE,"E111.53");
            var Q153;
            Q153=sQuery(id+"F0.wireOp",EDGE,"E111.54");
            var Q154;
            Q154=sQuery(id+"F0.wireOp",EDGE,"E56");
            var Q155;
            Q155=sQuery(id+"F0.wireOp",EDGE,"E111.31");
            var Q156;
            Q156=sQuery(id+"F0.wireOp",EDGE,"E102.MirrorCS");
            var Q157;
            Q157=sQuery(id+"F0.wireOp",EDGE,"E58.MirrorCS");
            var Q158;
            Q158=sQuery(id+"F0.wireOp",EDGE,"E25");
            var Q159;
            Q159=sQuery(id+"F0.wireOp",EDGE,"E67.MirrorCS");
            var Q160;
            Q160=sQuery(id+"F0.wireOp",EDGE,"E9");
            var Q161;
            Q161=sQuery(id+"F0.wireOp",EDGE,"E111.90");
            var Q162;
            Q162=sQuery(id+"F0.wireOp",EDGE,"E111.74");
            var Q163;
            Q163=sQuery(id+"F0.wireOp",EDGE,"E111.67");
            var Q164;
            Q164=sQuery(id+"F0.wireOp",EDGE,"E63.MirrorCS");
            var Q165;
            Q165=sQuery(id+"F0.wireOp",EDGE,"E111.33");
            var Q166;
            Q166=sQuery(id+"F0.wireOp",EDGE,"E105.MirrorCS");
            var Q167;
            Q167=sQuery(id+"F0.wireOp",EDGE,"E46");
            var Q168;
            Q168=sQuery(id+"F0.wireOp",EDGE,"E111.18");
            var Q169;
            Q169=sQuery(id+"F0.wireOp",EDGE,"E111.101");
            var Q170;
            Q170=sQuery(id+"F0.wireOp",EDGE,"E111.89");
            var Q171;
            Q171=sQuery(id+"F0.wireOp",EDGE,"E94.MirrorCS");
            var Q172;
            Q172=sQuery(id+"F0.wireOp",EDGE,"E76.MirrorCS");
            var Q173;
            Q173=sQuery(id+"F0.wireOp",EDGE,"E111.57");
            var Q174;
            Q174=sQuery(id+"F0.wireOp",EDGE,"E111.56");
            var Q175;
            Q175=sQuery(id+"F0.wireOp",EDGE,"E39");
            var Q176;
            Q176=sQuery(id+"F0.wireOp",EDGE,"E110.MirrorCS");
            var Q177;
            Q177=sQuery(id+"F0.wireOp",EDGE,"E109.MirrorCS");
            var Q178;
            Q178=sQuery(id+"F0.wireOp",EDGE,"E111.78");
            var Q179;
            Q179=sQuery(id+"F0.wireOp",EDGE,"E52");
            var Q180;
            Q180=sQuery(id+"F0.wireOp",EDGE,"E92.MirrorCS");
            var Q181;
            Q181=sQuery(id+"F0.wireOp",EDGE,"E111.41");
            var Q182;
            Q182=sQuery(id+"F0.wireOp",EDGE,"E111.5");
            var Q183;
            Q183=sQuery(id+"F0.wireOp",EDGE,"E40");
            var Q184;
            Q184=sQuery(id+"F0.wireOp",EDGE,"E111.36");
            var Q185;
            Q185=sQuery(id+"F0.wireOp",EDGE,"E41");
            var Q186;
            Q186=sQuery(id+"F0.wireOp",EDGE,"E5");
            var Q187;
            Q187=sQuery(id+"F0.wireOp",EDGE,"E12");
            var Q188;
            Q188=sQuery(id+"F0.wireOp",EDGE,"E51");
            var Q189;
            Q189=sQuery(id+"F0.wireOp",EDGE,"E59.MirrorCS");
            var Q190;
            Q190=sQuery(id+"F0.wireOp",EDGE,"E111.48");
            var Q191;
            Q191=sQuery(id+"F0.wireOp",EDGE,"E99.MirrorCS");
            var Q192;
            Q192=sQuery(id+"F0.wireOp",EDGE,"E50");
            var Q193;
            Q193=sQuery(id+"F0.wireOp",EDGE,"E111.59");
            var Q194;
            Q194=sQuery(id+"F0.wireOp",EDGE,"E15");
            var Q195;
            Q195=sQuery(id+"F0.wireOp",EDGE,"E111.96");
            var Q196;
            Q196=sQuery(id+"F0.wireOp",EDGE,"E111.58");
            var Q197;
            Q197=sQuery(id+"F0.wireOp",EDGE,"E111.0");
            var Q198;
            Q198=sQuery(id+"F0.wireOp",EDGE,"E14");
            var Q199;
            Q199=sQuery(id+"F0.wireOp",EDGE,"E0");
            var Q200;
            Q200=sQuery(id+"F0.wireOp",EDGE,"E57");
            var Q201;
            Q201=sQuery(id+"F0.wireOp",EDGE,"E93.MirrorCS");
            var Q202;
            Q202=sQuery(id+"F0.wireOp",EDGE,"E111.55");
            var Q203;
            Q203=sQuery(id+"F0.wireOp",EDGE,"E111.64");
            var Q204;
            Q204=sQuery(id+"F0.wireOp",EDGE,"E4");
            var Q205;
            Q205=sQuery(id+"F0.wireOp",EDGE,"E111.21");
            var Q206;
            Q206=sQuery(id+"F0.wireOp",EDGE,"E111.77");
            var Q207;
            Q207=sQuery(id+"F0.wireOp",EDGE,"E79.MirrorCS");
            var Q208;
            Q208=sQuery(id+"F0.wireOp",EDGE,"E26");
            var Q209;
            Q209=sQuery(id+"F0.wireOp",EDGE,"E3");
            var Q210;
            Q210=sQuery(id+"F0.wireOp",EDGE,"E1");
            var Q211;
            Q211=sQuery(id+"F0.wireOp",EDGE,"E28");
            var Q212;
            Q212=sQuery(id+"F0.wireOp",EDGE,"E111.63");
            extrude(context, id + "F1", {"entities" : qUnion([Q0]), "bodyType" : ToolBodyType.SURFACE, "operationType" : NewBodyOperationType.ADD, "surfaceEntities" : qUnion([Q1, Q2, Q3, Q4, Q5, Q6, Q7, Q8, Q9, Q10, Q11, Q12, Q13, Q14, Q15, Q16, Q17, Q18, Q19, Q20, Q21, Q22, Q23, Q24, Q25, Q26, Q27, Q28, Q29, Q30, Q31, Q32, Q33, Q34, Q35, Q36, Q37, Q38, Q39, Q40, Q41, Q42, Q43, Q44, Q45, Q46, Q47, Q48, Q49, Q50, Q51, Q52, Q53, Q54, Q55, Q56, Q57, Q58, Q59, Q60, Q61, Q62, Q63, Q64, Q65, Q66, Q67, Q68, Q69, Q70, Q71, Q72, Q73, Q74, Q75, Q76, Q77, Q78, Q79, Q80, Q81, Q82, Q83, Q84, Q85, Q86, Q87, Q88, Q89, Q90, Q91, Q92, Q93, Q94, Q95, Q96, Q97, Q98, Q99, Q100, Q101, Q102, Q103, Q104, Q105, Q106, Q107, Q108, Q109, Q110, Q111, Q112, Q113, Q114, Q115, Q116, Q117, Q118, Q119, Q120, Q121, Q122, Q123, Q124, Q125, Q126, Q127, Q128, Q129, Q130, Q131, Q132, Q133, Q134, Q135, Q136, Q137, Q138, Q139, Q140, Q141, Q142, Q143, Q144, Q145, Q146, Q147, Q148, Q149, Q150, Q151, Q152, Q153, Q154, Q155, Q156, Q157, Q158, Q159, Q160, Q161, Q162, Q163, Q164, Q165, Q166, Q167, Q168, Q169, Q170, Q171, Q172, Q173, Q174, Q175, Q176, Q177, Q178, Q179, Q180, Q181, Q182, Q183, Q184, Q185, Q186, Q187, Q188, Q189, Q190, Q191, Q192, Q193, Q194, Q195, Q196, Q197, Q198, Q199, Q200, Q201, Q202, Q203, Q204, Q205, Q206, Q207, Q208, Q209, Q210, Q211, Q212]), "depth" : 17.83 * mm, "offsetDistance" : 25.4 * mm});
        }
    });
